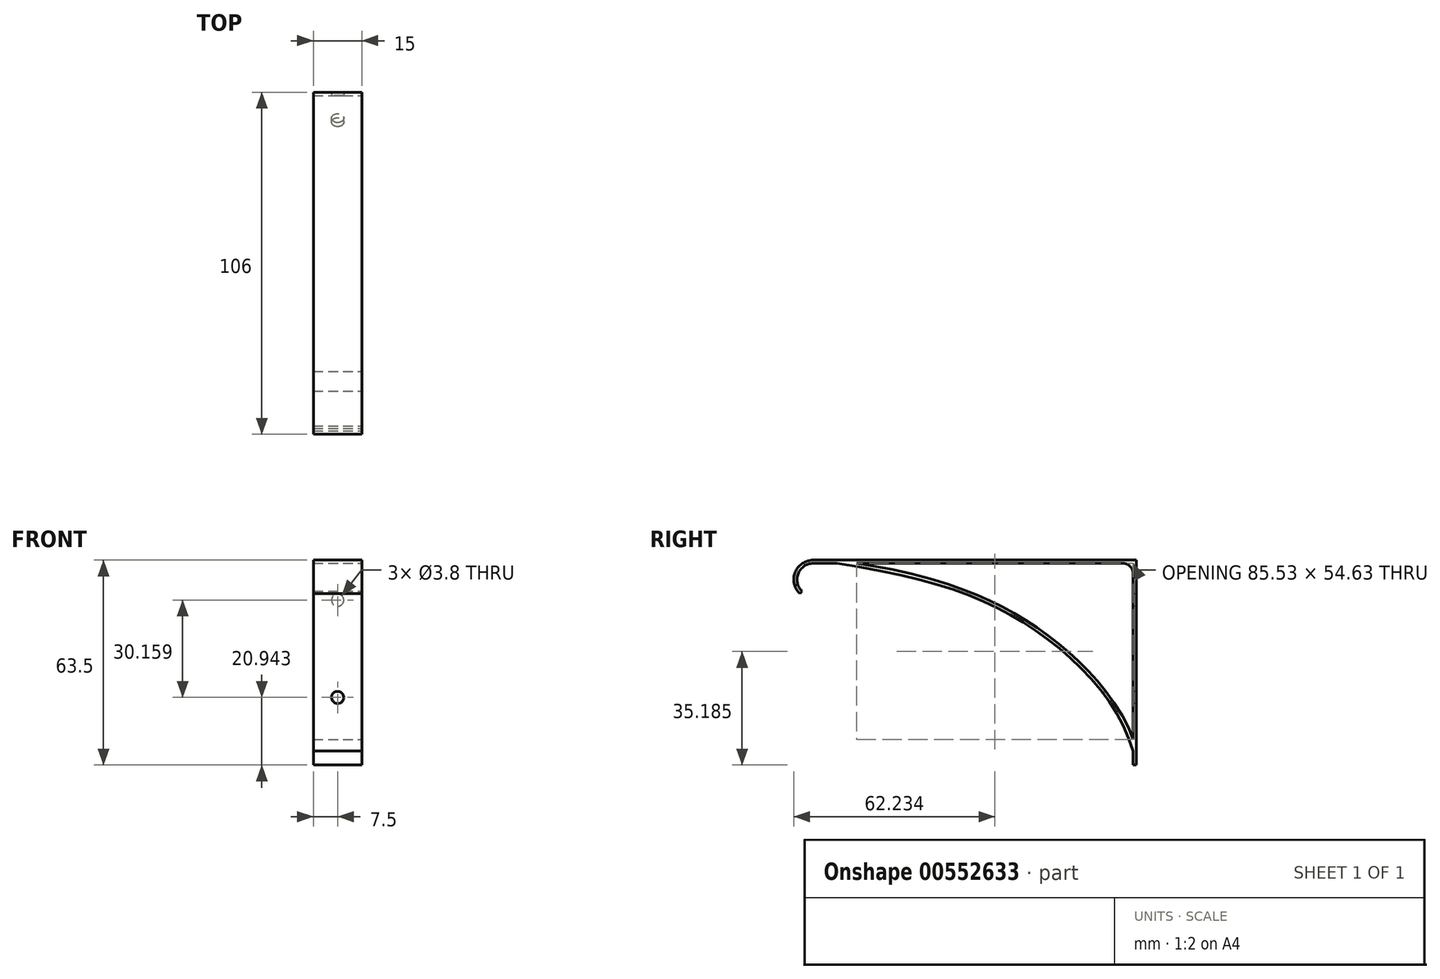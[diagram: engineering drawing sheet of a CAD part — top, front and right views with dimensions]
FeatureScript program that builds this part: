
annotation { "Feature Type Name" : "Feature", "Feature Type Description" : "" }
export const myFeature = defineFeature(function(context is Context, id is Id, definition is map)
    precondition{}
    {
        {
            var Q0;
            Q0=qCreatedBy(makeId("Front.planeOp"),FACE);
            var sketch = newSketch(context, id + "F0", { "sketchPlane" : qUnion([Q0])});
            skLineSegment(sketch, "E0.bottom", {"start": v(7.5, 0) * mm, "end": v(-7.5, 0) * mm});
            skLineSegment(sketch, "E0.top", {"start": v(7.5, -63.5) * mm, "end": v(-7.5, -63.5) * mm});
            skLineSegment(sketch, "E0.left", {"start": v(7.5, 0) * mm, "end": v(7.5, -63.5) * mm});
            skLineSegment(sketch, "E0.right", {"start": v(-7.5, 0) * mm, "end": v(-7.5, -63.5) * mm});
            skPoint(sketch, "E0.middle", {"position": v(0, -31.75) * mm});
            skSolve(sketch);
        }
        {
            var Q0;
            Q0 = qSketchRegion(id + "F0", true);
            extrude(context, id + "F1", {"entities" : qUnion([Q0]), "depth" : 1 * mm, "offsetDistance" : 25 * mm});
        }
        {
            var Q0;
            Q0=qCreatedBy(makeId("Top.planeOp"),FACE);
            var sketch = newSketch(context, id + "F2", { "sketchPlane" : qUnion([Q0])});
            skLineSegment(sketch, "E1.bottom", {"start": v(7.5, 0) * mm, "end": v(-7.5, 0) * mm});
            skLineSegment(sketch, "E1.top", {"start": v(7.5, -100) * mm, "end": v(-7.5, -100) * mm});
            skLineSegment(sketch, "E1.left", {"start": v(7.5, 0) * mm, "end": v(7.5, -100) * mm});
            skLineSegment(sketch, "E1.right", {"start": v(-7.5, 0) * mm, "end": v(-7.5, -100) * mm});
            skPoint(sketch, "E1.middle", {"position": v(0, -50) * mm});
            skSolve(sketch);
        }
        {
            var Q0;
            Q0 = qSketchRegion(id + "F2", true);
            extrude(context, id + "F3", {"entities" : qUnion([Q0]), "operationType" : NewBodyOperationType.ADD, "oppositeDirection" : true, "depth" : 1 * mm, "offsetDistance" : 25 * mm});
        }
        {
            var Q0;
            Q0=makeQuery(id+"F3.boolean.opBoolean","MERGE",FACE,{"derivedFrom":[makeQuery(id+"F1.opExtrude","SWEPT_FACE",FACE,{"disambiguationData":[OSD([sQuery(id+"F0.wireOp",EDGE,"E0.left")])]}),makeQuery(id+"F3.opExtrude","SWEPT_FACE",FACE,{"disambiguationData":[OSD([sQuery(id+"F2.wireOp",EDGE,"E1.left")])]})]});
            var sketch = newSketch(context, id + "F4", { "sketchPlane" : qUnion([Q0])});
            skFitSpline(sketch, "E2", {"points": [v(-1, -59.17) * mm, v(-28.67, -23.51) * mm, v(-92.68, -1) * mm], "startDerivative": vector(-25.13, 92.57) * mm, "endDerivative": vector(-167.72, 24.97) * mm});
            skFitSpline(sketch, "E3.0", {"points": [v(-0.13, -58.93) * mm, v(-1.2, -54.99) * mm, v(-3.69, -49.26) * mm, v(-8.35, -42.08) * mm, v(-12.43, -36.97) * mm, v(-16.98, -32.14) * mm, v(-21.9, -27.63) * mm, v(-27.11, -23.46) * mm, v(-32.5, -19.67) * mm, v(-38.12, -16.24) * mm, v(-44.1, -13.13) * mm, v(-50.5, -10.34) * mm, v(-59.75, -6.99) * mm, v(-72.87, -3.44) * mm, v(-85.54, -1.15) * mm, v(-92.55, -0.1) * mm]});
            skLineSegment(sketch, "E4", {"start": v(-92.55, -0.1) * mm, "end": v(-92.68, -1) * mm});
            skLineSegment(sketch, "E5", {"start": v(-1, -59.17) * mm, "end": v(-0.13, -58.93) * mm});
            skSolve(sketch);
        }
        {
            var Q0;
            Q0 = qSketchRegion(id + "F4", true);
            var Q1;
            Q1=makeQuery(id+"F3.boolean.opBoolean","MERGE",FACE,{"derivedFrom":[makeQuery(id+"F1.opExtrude","SWEPT_FACE",FACE,{"disambiguationData":[OSD([sQuery(id+"F0.wireOp",EDGE,"E0.right")])]}),makeQuery(id+"F3.opExtrude","SWEPT_FACE",FACE,{"disambiguationData":[OSD([sQuery(id+"F2.wireOp",EDGE,"E1.right")])]})]});
            extrude(context, id + "F5", {"entities" : qUnion([Q0]), "operationType" : NewBodyOperationType.ADD, "endBound" : BoundingType.UP_TO_SURFACE, "oppositeDirection" : true, "depth" : 25 * mm, "endBoundEntityFace" : qUnion([Q1]), "offsetDistance" : 25 * mm});
        }
        {
            var Q0;
            {var subQ1=sQuery(id+"F0.wireOp",EDGE,"E0.right");var subQ3=sQuery(id+"F0.wireOp",EDGE,"E0.left");var subQ4=sQuery(id+"F4.wireOp",EDGE,"E3.0");Q0=makeQuery(id+"F5.boolean.opBoolean","SPLIT",FACE,{"disambiguationData":[TD([makeQuery(id+"F5.opExtrude","SWEPT_FACE",FACE,{"disambiguationData":[OSD([subQ4])]})])],"derivedFrom":makeQuery(id+"F1.opExtrude","CAP_FACE",FACE,{"disambiguationData":[OSD([sQuery(id+"F0.wireOp",EDGE,"E0.bottom"),sQuery(id+"F0.wireOp",EDGE,"E0.top"),subQ3,subQ1])],"isStart":false})});}
            var sketch = newSketch(context, id + "F6", { "sketchPlane" : qUnion([Q0])});
            skPoint(sketch, "E6", {"position": v(0, -12.4) * mm});
            skPoint(sketch, "E7", {"position": v(0, -42.56) * mm});
            skSolve(sketch);
        }
        {
            var Q0;
            Q0=sQuery(id+"F6.wireOp",VERTEX,"E6");
            var Q1;
            Q1=makeQuery(id+"F1.opExtrude","SWEPT_BODY",BODY,{"disambiguationData":[OSD([sQuery(id+"F0.wireOp",EDGE,"E0.bottom"),sQuery(id+"F0.wireOp",EDGE,"E0.top"),sQuery(id+"F0.wireOp",EDGE,"E0.left"),sQuery(id+"F0.wireOp",EDGE,"E0.right")])]});
            hole(context, id + "F7", {"style" : HoleStyle.SIMPLE, "endStyle" : HoleEndStyle.THROUGH, "standardTappedOrClearance" : lookupTablePath({ "standard" : "ANSI", "fit" : "Normal (ASME)", "size" : "#6", "type" : "Clearance" }), "standardBlindInLast" : lookupTablePath({ "fit" : "Free", "standard" : "ANSI", "size" : "#6", "type" : "Clearance" }), "holeDiameter" : 3.8 * mm, "isTappedThrough" : true, "tappedDepth" : 12 * mm, "tapClearance" : 3, "locations" : qUnion([Q0]), "scope" : qUnion([Q1])});
        }
        {
            var Q0;
            Q0=sQuery(id+"F6.wireOp",VERTEX,"E7");
            var Q1;
            Q1=makeQuery(id+"F1.opExtrude","SWEPT_BODY",BODY,{"disambiguationData":[OSD([sQuery(id+"F0.wireOp",EDGE,"E0.bottom"),sQuery(id+"F0.wireOp",EDGE,"E0.top"),sQuery(id+"F0.wireOp",EDGE,"E0.left"),sQuery(id+"F0.wireOp",EDGE,"E0.right")])]});
            hole(context, id + "F8", {"style" : HoleStyle.SIMPLE, "endStyle" : HoleEndStyle.THROUGH, "oppositeDirection" : true, "standardTappedOrClearance" : lookupTablePath({ "standard" : "ANSI", "fit" : "Normal (ASME)", "size" : "#6", "type" : "Clearance" }), "standardBlindInLast" : lookupTablePath({ "fit" : "Free", "standard" : "ANSI", "size" : "#6", "type" : "Clearance" }), "holeDiameter" : 3.8 * mm, "isTappedThrough" : true, "tappedDepth" : 12 * mm, "tapClearance" : 3, "locations" : qUnion([Q0]), "scope" : qUnion([Q1])});
        }
        {
            var Q0;
            Q0=sQuery(id+"F6.wireOp",VERTEX,"E7");
            var Q1;
            Q1=makeQuery(id+"F1.opExtrude","SWEPT_BODY",BODY,{"disambiguationData":[OSD([sQuery(id+"F0.wireOp",EDGE,"E0.bottom"),sQuery(id+"F0.wireOp",EDGE,"E0.top"),sQuery(id+"F0.wireOp",EDGE,"E0.left"),sQuery(id+"F0.wireOp",EDGE,"E0.right")])]});
            hole(context, id + "F9", {"style" : HoleStyle.SIMPLE, "endStyle" : HoleEndStyle.THROUGH, "standardTappedOrClearance" : lookupTablePath({ "standard" : "ANSI", "fit" : "Normal (ASME)", "size" : "#6", "type" : "Clearance" }), "standardBlindInLast" : lookupTablePath({ "fit" : "Free", "standard" : "ANSI", "size" : "#6", "type" : "Clearance" }), "holeDiameter" : 3.8 * mm, "isTappedThrough" : true, "tappedDepth" : 12 * mm, "tapClearance" : 3, "locations" : qUnion([Q0]), "scope" : qUnion([Q1])});
        }
        {
            var Q0;
            Q0=makeQuery(id+"F3.boolean.opBoolean","INTERSECT",EDGE,{"derivedFrom":[makeQuery(id+"F1.opExtrude","CAP_FACE",FACE,{"disambiguationData":[OSD([sQuery(id+"F0.wireOp",EDGE,"E0.bottom"),sQuery(id+"F0.wireOp",EDGE,"E0.top"),sQuery(id+"F0.wireOp",EDGE,"E0.left"),sQuery(id+"F0.wireOp",EDGE,"E0.right")])],"isStart":false}),makeQuery(id+"F3.opExtrude","CAP_FACE",FACE,{"disambiguationData":[OSD([sQuery(id+"F2.wireOp",EDGE,"E1.bottom"),sQuery(id+"F2.wireOp",EDGE,"E1.top"),sQuery(id+"F2.wireOp",EDGE,"E1.left"),sQuery(id+"F2.wireOp",EDGE,"E1.right")])],"isStart":false})]});
            fillet(context, id + "F10", {"entities" : qUnion([Q0]), "radius" : 3 * mm, "tangentPropagation" : true, "allowEdgeOverflow" : false});
        }
        {
            var Q0;
            Q0=makeQuery(id+"F5.boolean.opBoolean","MERGE",FACE,{"derivedFrom":[makeQuery(id+"F3.boolean.opBoolean","MERGE",FACE,{"derivedFrom":[makeQuery(id+"F1.opExtrude","SWEPT_FACE",FACE,{"disambiguationData":[OSD([sQuery(id+"F0.wireOp",EDGE,"E0.left")])]}),makeQuery(id+"F3.opExtrude","SWEPT_FACE",FACE,{"disambiguationData":[OSD([sQuery(id+"F2.wireOp",EDGE,"E1.left")])]})]}),makeQuery(id+"F5.opExtrude","CAP_FACE",FACE,{"disambiguationData":[OSD([sQuery(id+"F4.wireOp",EDGE,"E2"),sQuery(id+"F4.wireOp",EDGE,"E3.0"),sQuery(id+"F4.wireOp",EDGE,"E4"),sQuery(id+"F4.wireOp",EDGE,"E5")])],"isStart":true})]});
            var sketch = newSketch(context, id + "F11", { "sketchPlane" : qUnion([Q0])});
            skArc(sketch, "E8", {"start": v(-100, 0) * mm, "mid": v(-105.57, -3.78) * mm, "end": v(-104.13, -10.35) * mm});
            skArc(sketch, "E9.0", {"start": v(-100, -1) * mm, "mid": v(-104.64, -4.15) * mm, "end": v(-103.44, -9.63) * mm});
            skLineSegment(sketch, "E10", {"start": v(-103.44, -9.63) * mm, "end": v(-104.13, -10.35) * mm});
            skSolve(sketch);
        }
        {
            var Q0;
            Q0=makeQuery(id+"F11.imprint","IMPRINT",FACE,{"disambiguationData":[TD([[makeQuery(id+"F11.imprint","IMPRINT",EDGE,{"derivedFrom":sQuery(id+"F11.wireOp",EDGE,"E8")}),1.0]])]});
            var Q1;
            {var subQ0=sQuery(id+"F2.wireOp",EDGE,"E1.right");var subQ1=sQuery(id+"F0.wireOp",EDGE,"E0.right");Q1=makeQuery(id+"F5.boolean.opBoolean","MERGE",FACE,{"derivedFrom":[makeQuery(id+"F3.boolean.opBoolean","MERGE",FACE,{"derivedFrom":[makeQuery(id+"F1.opExtrude","SWEPT_FACE",FACE,{"disambiguationData":[OSD([subQ1])]}),makeQuery(id+"F3.opExtrude","SWEPT_FACE",FACE,{"disambiguationData":[OSD([subQ0])]})]}),makeQuery(id+"F5.opExtrude","CAP_FACE",FACE,{"disambiguationData":[OSD([subQ1,subQ0])],"isStart":false})]});}
            extrude(context, id + "F12", {"entities" : qUnion([Q0]), "operationType" : NewBodyOperationType.ADD, "endBound" : BoundingType.UP_TO_SURFACE, "oppositeDirection" : true, "depth" : 25 * mm, "endBoundEntityFace" : qUnion([Q1]), "offsetDistance" : 25 * mm});
        }
    });
